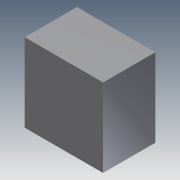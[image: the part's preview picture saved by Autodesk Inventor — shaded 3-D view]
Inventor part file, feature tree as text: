
AUTODESK INVENTOR PART (.ipt)
format: ipt  version: 2011 (Build 150239000, 239)  size: 68,608 bytes
history: native  units: in
note: dims shown in document units (in); Inventor stores cm internally (conversion verified against a paired STEP export)
features: extrude x1, sketch x1
ambient origin geometry x8: Origin, YZ Plane, XZ Plane, XY Plane, X Axis, Y Axis, Z Axis, Center Point
bodies: Solid1 (feature_tree)
feature tree (2):
  extrude  "Extrusion1"  Depth=10.5in
  sketch  "Sketch1"  dims[d0=10.5in d1=10.5in d2=7.0in d3=0.0in]
